# Revit family: 602-1-002-DN40-50
name_source: partatom
category: Pipe Accessories
units: mm (PartAtom-declared; Revit-internal decimal feet)

## family parameters
Always vertical = Yes
Cut with Voids When Loaded = No
Part Type = Valve - Breaks Into
Round Connector Dimension = Use Diameter
Shared = No
Work Plane-Based = No

## types (4) — shared parameters
DN40 - 50_46-63 = 602-063-074-6100
DN40 - 65_46-63 = 602-063-085-6100
DN50 - 65_57-74 = 602-074-085-6100
DN50 - 80_57-74 = 602-074-106-6100
Description_ = AVK UNIVERSAL SUPA® STEP COUPLING
L = 217 mm  [stored 0.711942 ft]
L1 = 100 mm  [stored 0.328084 ft]
PCD = 137 mm  [stored 0.449475 ft]
Search_table = 602-1-002-DN40-50
URL_product_pages = https://www.avkvalves.com

## per-type parameters (varying)
| type | DN | DN2 | DN3 | DN_Ref | DN_Ref_2 | ID | Side_length |
| DN40 - 50_46-63 | 41 mm | 74 mm  [stored 0.242782 ft] | 63 mm  [stored 0.206693 ft] | 37 mm  [stored 0.121391 ft] | 32 mm | 20 mm | 163 mm  [stored 0.534777 ft] |
| DN40 - 65_46-63 | 41 mm | 85 mm  [stored 0.278871 ft] | 63 mm  [stored 0.206693 ft] | 43 mm | 32 mm | 20 mm | 163 mm  [stored 0.534777 ft] |
| DN50 - 65_57-74 | 51 mm | 85 mm  [stored 0.278871 ft] | 74 mm  [stored 0.242782 ft] | 43 mm | 37 mm  [stored 0.121391 ft] | 25 mm  [stored 0.082021 ft] | 174 mm  [stored 0.570866 ft] |
| DN50 - 80_57-74 | 51 mm | 90 mm  [stored 0.295276 ft] | 74 mm  [stored 0.242782 ft] | 45 mm  [stored 0.147638 ft] | 37 mm  [stored 0.121391 ft] | 25 mm  [stored 0.082021 ft] | 174 mm  [stored 0.570866 ft] |

note: [stored X ft] marks values corroborated as IEEE doubles in the binary element streams (Revit-internal decimal feet)

## geometry (parser evidence)
native form markers: Sweep x10
no freeform markers — native parametric forms only
